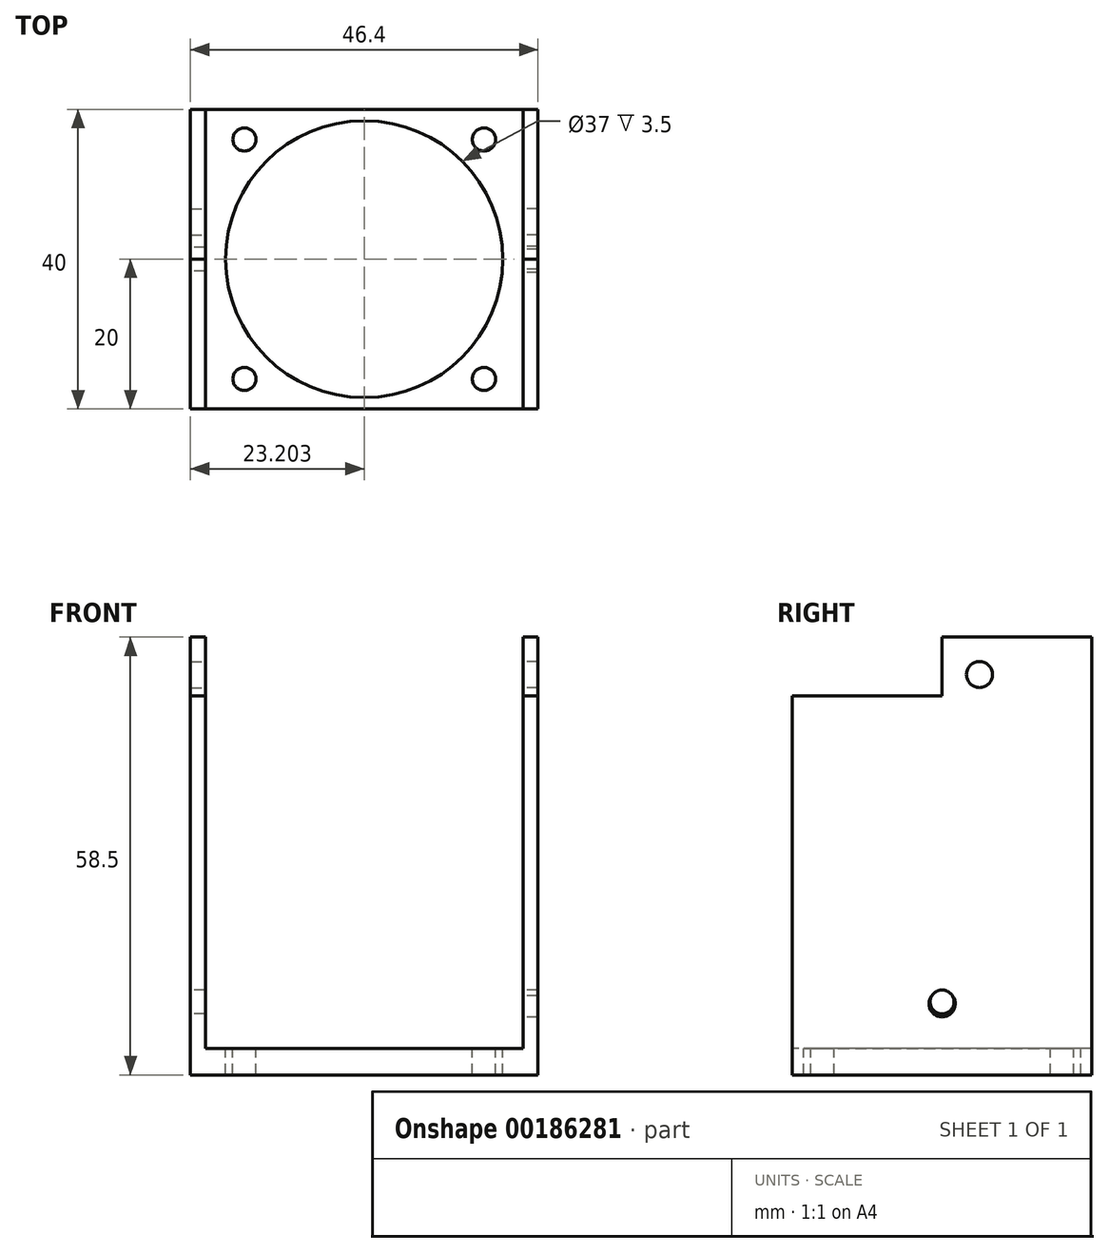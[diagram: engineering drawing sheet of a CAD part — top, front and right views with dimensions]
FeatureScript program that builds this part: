
annotation { "Feature Type Name" : "Feature", "Feature Type Description" : "" }
export const myFeature = defineFeature(function(context is Context, id is Id, definition is map)
    precondition{}
    {
        {
            var Q0;
            Q0=qCreatedBy(makeId("Top.planeOp"),FACE);
            var sketch = newSketch(context, id + "F0", { "sketchPlane" : qUnion([Q0])});
            skLineSegment(sketch, "E0.bottom", {"start": v(-12.6, 20) * mm, "end": v(32.4, 20) * mm});
            skLineSegment(sketch, "E0.top", {"start": v(-12.6, -20) * mm, "end": v(32.4, -20) * mm});
            skLineSegment(sketch, "E0.left", {"start": v(-12.6, 20) * mm, "end": v(-12.6, -20) * mm});
            skLineSegment(sketch, "E0.right", {"start": v(32.4, 20) * mm, "end": v(32.4, -20) * mm});
            skPoint(sketch, "E1", {"position": v(9.9, 0) * mm});
            skCircle(sketch, "E2", {"center": v(9.9, 0) * mm, "radius": 18.5 * mm});
            skPoint(sketch, "E3", {"position": v(25.9, 16) * mm});
            skPoint(sketch, "E4", {"position": v(-6.1, 16) * mm});
            skPoint(sketch, "E5", {"position": v(-6.1, -16) * mm});
            skPoint(sketch, "E6", {"position": v(25.9, -16) * mm});
            skCircle(sketch, "E7", {"center": v(-6.1, 16) * mm, "radius": 1.55 * mm});
            skCircle(sketch, "E8", {"center": v(25.9, 16) * mm, "radius": 1.55 * mm});
            skCircle(sketch, "E9", {"center": v(25.9, -16) * mm, "radius": 1.55 * mm});
            skCircle(sketch, "E10", {"center": v(-6.1, -16) * mm, "radius": 1.55 * mm});
            skPoint(sketch, "E11", {"position": v(-11.3, 20) * mm});
            skPoint(sketch, "E12", {"position": v(-11.3, -20) * mm});
            skPoint(sketch, "E13", {"position": v(31.1, -20) * mm});
            skPoint(sketch, "E14", {"position": v(31.1, 20) * mm});
            skLineSegment(sketch, "E15", {"start": v(-11.3, 20) * mm, "end": v(-11.3, -20) * mm});
            skLineSegment(sketch, "E16", {"start": v(31.1, 20) * mm, "end": v(31.1, -20) * mm});
            skSolve(sketch);
        }
        {
            var Q0;
            Q0=makeQuery(id+"F0.imprint","IMPRINT",FACE,{"disambiguationData":[TD([[makeQuery(id+"F0.imprint","IMPRINT",EDGE,{"derivedFrom":sQuery(id+"F0.wireOp",EDGE,"E2")}),-1.0]])]});
            var Q1;
            {var subQ0=sQuery(id+"F0.wireOp",EDGE,"E0.left");Q1=makeQuery(id+"F0.imprint","IMPRINT",FACE,{"disambiguationData":[TD([[makeQuery(id+"F0.imprint","IMPRINT",EDGE,{"derivedFrom":subQ0}),1.0]])]});}
            var Q2;
            {var subQ0=sQuery(id+"F0.wireOp",EDGE,"E0.right");Q2=makeQuery(id+"F0.imprint","IMPRINT",FACE,{"disambiguationData":[TD([[makeQuery(id+"F0.imprint","IMPRINT",EDGE,{"derivedFrom":subQ0}),-1.0]])]});}
            extrude(context, id + "F1", {"entities" : qUnion([Q0, Q1, Q2]), "oppositeDirection" : true, "depth" : 3.5 * mm});
        }
        {
            var Q0;
            Q0=makeQuery(id+"F1.opExtrude","CAP_FACE",FACE,{"disambiguationData":[OSD([sQuery(id+"F0.wireOp",EDGE,"E0.bottom"),sQuery(id+"F0.wireOp",EDGE,"E0.top"),sQuery(id+"F0.wireOp",EDGE,"E0.left"),sQuery(id+"F0.wireOp",EDGE,"E0.right"),sQuery(id+"F0.wireOp",EDGE,"E2"),sQuery(id+"F0.wireOp",EDGE,"E7"),sQuery(id+"F0.wireOp",EDGE,"E8"),sQuery(id+"F0.wireOp",EDGE,"E9"),sQuery(id+"F0.wireOp",EDGE,"E10")])],"isStart":true});
            var sketch = newSketch(context, id + "F2", { "sketchPlane" : qUnion([Q0])});
            skPoint(sketch, "E17", {"position": v(31.1, 20) * mm});
            skPoint(sketch, "E18", {"position": v(31.1, -20) * mm});
            skPoint(sketch, "E19", {"position": v(-11.3, 20) * mm});
            skPoint(sketch, "E20", {"position": v(-11.3, -20) * mm});
            skLineSegment(sketch, "E21", {"start": v(-11.3, 20) * mm, "end": v(-11.3, -20) * mm});
            skLineSegment(sketch, "E22", {"start": v(31.1, -20) * mm, "end": v(31.1, 20) * mm});
            skSolve(sketch);
        }
        {
            var Q0;
            {var subQ0=sQuery(id+"F2.wireOp",EDGE,"E21");Q0=makeQuery(id+"F2.imprint","IMPRINT",FACE,{"disambiguationData":[TD([[makeQuery(id+"F2.imprint","IMPRINT",EDGE,{"derivedFrom":subQ0}),-1.0]])]});}
            var Q1;
            {var subQ0=sQuery(id+"F2.wireOp",EDGE,"E22");Q1=makeQuery(id+"F2.imprint","IMPRINT",FACE,{"disambiguationData":[TD([[makeQuery(id+"F2.imprint","IMPRINT",EDGE,{"derivedFrom":subQ0}),-1.0]])]});}
            extrude(context, id + "F3", {"entities" : qUnion([Q0, Q1]), "operationType" : NewBodyOperationType.ADD, "depth" : 55 * mm});
        }
        {
            var Q0;
            Q0=makeQuery(id+"F3.opExtrude","SWEPT_FACE",FACE,{"disambiguationData":[OSD([sQuery(id+"F2.wireOp",EDGE,"E21")])]});
            var sketch = newSketch(context, id + "F4", { "sketchPlane" : qUnion([Q0])});
            skPoint(sketch, "E23", {"position": v(5, 50) * mm});
            skPoint(sketch, "E24", {"position": v(-14, 50) * mm});
            skPoint(sketch, "E25", {"position": v(0, 6) * mm});
            skPoint(sketch, "E25.positionSnap0", {"position": v(0, 0) * mm});
            skPoint(sketch, "E26", {"position": v(-32.85, 72.44) * mm});
            skCircle(sketch, "E27", {"center": v(-14, 50) * mm, "radius": 1.75 * mm});
            skCircle(sketch, "E28", {"center": v(5, 50) * mm, "radius": 1.75 * mm});
            skCircle(sketch, "E29", {"center": v(0, 6) * mm, "radius": 1.75 * mm});
            skSolve(sketch);
        }
        {
            var Q0;
            Q0=makeQuery(id+"F3.opExtrude","SWEPT_FACE",FACE,{"disambiguationData":[OSD([sQuery(id+"F2.wireOp",EDGE,"E22")])]});
            var sketch = newSketch(context, id + "F5", { "sketchPlane" : qUnion([Q0])});
            skPoint(sketch, "E30", {"position": v(5, 50) * mm});
            skPoint(sketch, "E31", {"position": v(-5, 50) * mm});
            skPoint(sketch, "E32", {"position": v(0, 6) * mm});
            skSolve(sketch);
        }
        {
            var Q0;
            Q0=sQuery(id+"F4.wireOp",VERTEX,"E23");
            var Q1;
            Q1=sQuery(id+"F4.wireOp",VERTEX,"E24");
            var Q2;
            Q2=sQuery(id+"F4.wireOp",VERTEX,"E25");
            var Q3;
            Q3=makeQuery(id+"F1.opExtrude","SWEPT_BODY",BODY,{"disambiguationData":[OSD([sQuery(id+"F0.wireOp",EDGE,"E0.bottom"),sQuery(id+"F0.wireOp",EDGE,"E0.top"),sQuery(id+"F0.wireOp",EDGE,"E0.left"),sQuery(id+"F0.wireOp",EDGE,"E0.right"),sQuery(id+"F0.wireOp",EDGE,"E2"),sQuery(id+"F0.wireOp",EDGE,"E7"),sQuery(id+"F0.wireOp",EDGE,"E8"),sQuery(id+"F0.wireOp",EDGE,"E9"),sQuery(id+"F0.wireOp",EDGE,"E10")])]});
            hole(context, id + "F6", {"style" : HoleStyle.SIMPLE, "endStyle" : HoleEndStyle.THROUGH, "oppositeDirection" : true, "holeDiameter" : 3.5 * mm, "tappedDepth" : 12 * mm, "tapClearance" : 3, "startFromSketch" : true, "locations" : qUnion([Q0, Q1, Q2]), "scope" : qUnion([Q3])});
        }
        {
            var Q0;
            {var subQ0=sQuery(id+"F0.wireOp",EDGE,"E0.right");Q0=makeQuery(id+"F3.boolean.opBoolean","MERGE",FACE,{"derivedFrom":[makeQuery(id+"F1.opExtrude","SWEPT_FACE",FACE,{"disambiguationData":[OSD([subQ0])]}),makeQuery(id+"F3.opExtrude","SWEPT_FACE",FACE,{"disambiguationData":[OSD([subQ0])]})]});}
            extrude(context, id + "F7", {"entities" : qUnion([Q0]), "operationType" : NewBodyOperationType.ADD, "depth" : 0.7 * mm});
        }
        {
            var Q0;
            {var subQ0=sQuery(id+"F0.wireOp",EDGE,"E0.left");Q0=makeQuery(id+"F3.boolean.opBoolean","MERGE",FACE,{"derivedFrom":[makeQuery(id+"F1.opExtrude","SWEPT_FACE",FACE,{"disambiguationData":[OSD([subQ0])]}),makeQuery(id+"F3.opExtrude","SWEPT_FACE",FACE,{"disambiguationData":[OSD([subQ0])]})]});}
            extrude(context, id + "F8", {"entities" : qUnion([Q0]), "operationType" : NewBodyOperationType.ADD, "depth" : 0.7 * mm});
        }
        {
            var Q0;
            Q0=makeQuery(id+"F8.opExtrude","CAP_FACE",FACE,{"disambiguationData":[OSD([sQuery(id+"F0.wireOp",EDGE,"E0.left")])],"isStart":false});
            var sketch = newSketch(context, id + "F9", { "sketchPlane" : qUnion([Q0])});
            skPoint(sketch, "E33", {"position": v(0, 55) * mm});
            skPoint(sketch, "E34", {"position": v(20, 47.17) * mm});
            skLineSegment(sketch, "E35", {"start": v(20, 47.17) * mm, "end": v(0, 47.17) * mm});
            skLineSegment(sketch, "E36", {"start": v(0, 47.17) * mm, "end": v(0, 55) * mm});
            skSolve(sketch);
        }
        {
            var Q0;
            {var subQ5=sQuery(id+"F9.wireOp",EDGE,"E35");Q0=makeQuery(id+"F9.imprint","IMPRINT",FACE,{"disambiguationData":[TD([[makeQuery(id+"F9.imprint","IMPRINT",EDGE,{"derivedFrom":subQ5}),-1.0]])]});}
            extrude(context, id + "F10", {"entities" : qUnion([Q0]), "operationType" : NewBodyOperationType.REMOVE, "oppositeDirection" : true, "depth" : 60 * mm});
        }
        {
            var Q0;
            Q0=sQuery(id+"F5.wireOp",VERTEX,"E31");
            var Q1;
            Q1=makeQuery(id+"F1.opExtrude","SWEPT_BODY",BODY,{"disambiguationData":[OSD([sQuery(id+"F0.wireOp",EDGE,"E0.bottom"),sQuery(id+"F0.wireOp",EDGE,"E0.top"),sQuery(id+"F0.wireOp",EDGE,"E0.left"),sQuery(id+"F0.wireOp",EDGE,"E0.right"),sQuery(id+"F0.wireOp",EDGE,"E2"),sQuery(id+"F0.wireOp",EDGE,"E7"),sQuery(id+"F0.wireOp",EDGE,"E8"),sQuery(id+"F0.wireOp",EDGE,"E9"),sQuery(id+"F0.wireOp",EDGE,"E10")])]});
            hole(context, id + "F11", {"style" : HoleStyle.SIMPLE, "endStyle" : HoleEndStyle.THROUGH, "oppositeDirection" : true, "holeDiameter" : 3.5 * mm, "tappedDepth" : 12 * mm, "tapClearance" : 3, "startFromSketch" : true, "locations" : qUnion([Q0]), "scope" : qUnion([Q1])});
        }
        {
            var Q0;
            Q0=makeQuery(id+"F8.opExtrude","CAP_FACE",FACE,{"disambiguationData":[OSD([sQuery(id+"F0.wireOp",EDGE,"E0.left")])],"isStart":false});
            var sketch = newSketch(context, id + "F12", { "sketchPlane" : qUnion([Q0])});
            skCircle(sketch, "E37", {"center": v(0, 6.26) * mm, "radius": 1.6 * mm});
            skSolve(sketch);
        }
        {
            var Q0;
            Q0=makeQuery(id+"F12.imprint","IMPRINT",FACE,{"disambiguationData":[TD([[makeQuery(id+"F12.imprint","IMPRINT",EDGE,{"derivedFrom":sQuery(id+"F12.wireOp",EDGE,"E37")}),1.0]])]});
            extrude(context, id + "F13", {"entities" : qUnion([Q0]), "operationType" : NewBodyOperationType.REMOVE, "oppositeDirection" : true, "depth" : 60 * mm});
        }
    });
